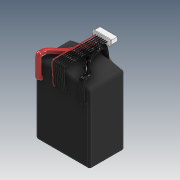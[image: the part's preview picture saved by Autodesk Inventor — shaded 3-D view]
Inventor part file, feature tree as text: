
AUTODESK INVENTOR PART (.ipt)
format: ipt  version: 2020 (Build 240168000, 168)  size: 946,176 bytes
history: native  units: mm
features: sketch x15, extrude x8, plane x5, sweep x2, projected_geometry x2, pattern_linear x1, fillet x1, mirror x1
ambient origin geometry x8: Origin, YZ Plane, XZ Plane, XY Plane, X Axis, Y Axis, Z Axis, Center Point
bodies: Solid1 (feature_tree)
feature tree (35):
  extrude  "Extrusion1"  Depth=36.0mm TaperAngle=0.0deg
  plane  "Work Plane1"
  sketch  "Sketch2"  dims[d5=-80.0mm d6=0.0mm d7=35.0mm d8=7.0mm d9=7.28011mm]
  plane  "Work Plane2"
  plane  "Work Plane3"
  extrude  "Extrusion7"  Depth=35.0mm TaperAngle=0.0deg
  extrude  "Extrusion8"  Depth=24.0mm
  sketch  "Sketch12"  dims[d45=18.0mm d46=19.0mm d47=7.69mm d49=1.0mm d50=40.0mm d51=4.0mm d52=0.0mm]
  plane  "Work Plane4"
  sweep  "Sweep2"
  pattern_linear  "Rectangular Pattern1"  Count1=4  [1 undecoded]
  fillet  "Fillet1"  Radius=4.0mm
  sketch  "Sketch16"  dims[d62=1.0mm d63=0.0mm d64=0.0mm]
  sketch  "Sketch17"  dims[d65=70.0mm d67=2.0mm d68=2.0mm]
  plane  "Work Plane6"
  sweep  "Sweep3"
  mirror  "Mirror2"
  extrude  "Extrusion14"  TaperAngle=90.0deg  [1 undecoded]
  extrude  "Extrusion15"  TaperAngle=0.0deg  [1 undecoded]
  extrude  "Extrusion16"  Depth=2.0mm
  extrude  "Extrusion17"  Depth=45.0mm
  extrude  "Extrusion18"  TaperAngle=0.0deg  [1 undecoded]
  sketch  "Sketch1"  dims[d0=75.0mm d1=56.0mm d2=200.0mm d3=36.0mm d4=0.0mm]
  sketch  "Sketch10"  dims[d10=10.671981mm d11=24.0mm]
  sketch  "Sketch11"  dims[d12=33.103896mm d44=-84.0mm]
  sketch  "Sketch13"  dims[d53=1.0mm d54=5.0mm d55=0.0mm d56=0.0mm d57=6.0mm]
  sketch  "Sketch14"  dims[d60=2.0mm d61=90.0deg]
  sketch  "Sketch18"  dims[d73=5.0mm d74=45.0mm]
  sketch  "Sketch25"  dims[d75=15.0mm d76=0.0mm d77=0.0mm]
  projected_geometry  "Projected Loop2"
  sketch  "Sketch26"  dims[d104=8.0mm d105=16.0mm d106=3.5mm d107=11.0mm d108=2.0mm]
  projected_geometry  "Projected Loop3"
  sketch  "Sketch27"  dims[d109=8.0mm d110=0.0mm]
  sketch  "Sketch28"  dims[d111=8.0mm d112=0.0mm]
  sketch  "Sketch29"  dims[d113=8.0mm d114=1.0mm d115=2.0mm d116=8.0mm d117=0.0mm d118=1.0mm d119=4.0mm d120=1.0mm d121=1.0mm d122=0.0mm d123=3.5mm d124=3.5mm d125=1.0mm d126=8.0mm d127=0.0mm]
note: 4 required parameter values undecoded (feature->parameter linkage not recoverable at this tier; creation-order binding heuristic only, values carry confidence <= 0.55)
